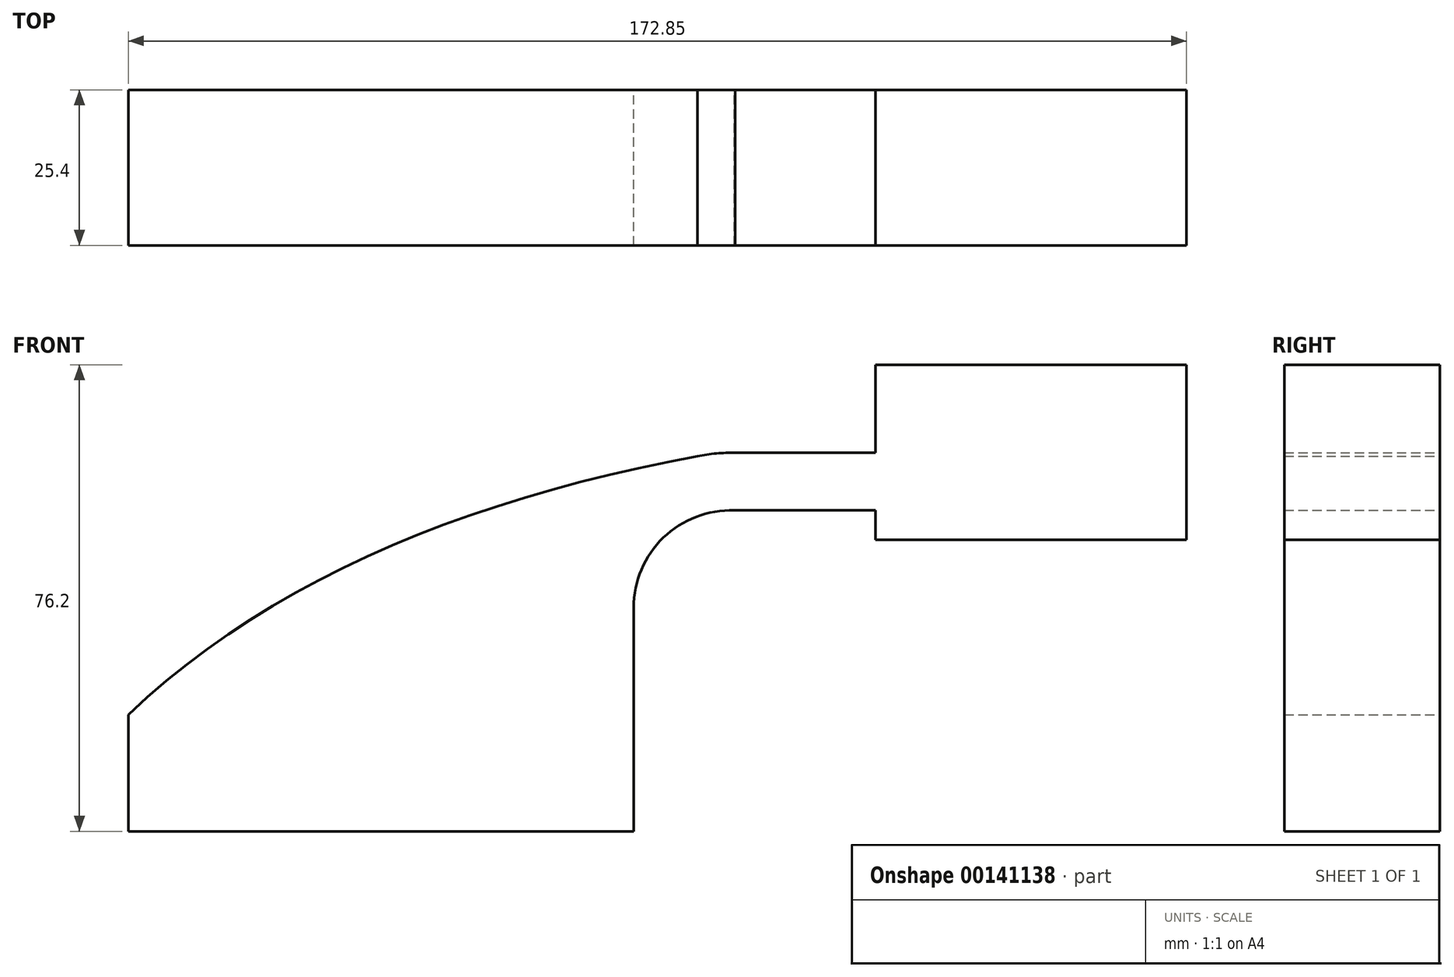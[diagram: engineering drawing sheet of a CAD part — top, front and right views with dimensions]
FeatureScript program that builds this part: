
annotation { "Feature Type Name" : "Feature", "Feature Type Description" : "" }
export const myFeature = defineFeature(function(context is Context, id is Id, definition is map)
    precondition{}
    {
        {
            var Q0;
            Q0=qCreatedBy(makeId("Front.planeOp"),FACE);
            var sketch = newSketch(context, id + "F0", { "sketchPlane" : qUnion([Q0])});
            skLineSegment(sketch, "E0.bottom", {"start": v(0, 0) * mm, "end": v(-82.55, 0) * mm});
            skLineSegment(sketch, "E0.top", {"start": v(0, 19.05) * mm, "end": v(-82.55, 19.05) * mm});
            skLineSegment(sketch, "E0.left", {"start": v(0, 0) * mm, "end": v(0, 19.05) * mm});
            skLineSegment(sketch, "E0.right", {"start": v(-82.55, 0) * mm, "end": v(-82.55, 19.05) * mm});
            skLineSegment(sketch, "E1.bottom", {"start": v(39.5, 47.63) * mm, "end": v(90.3, 47.63) * mm});
            skLineSegment(sketch, "E1.top", {"start": v(39.5, 76.2) * mm, "end": v(90.3, 76.2) * mm});
            skLineSegment(sketch, "E1.left", {"start": v(39.5, 47.63) * mm, "end": v(39.5, 76.2) * mm});
            skLineSegment(sketch, "E1.right", {"start": v(90.3, 47.63) * mm, "end": v(90.3, 76.2) * mm});
            skLineSegment(sketch, "E2", {"start": v(0, 19.05) * mm, "end": v(0, 36.54) * mm});
            skArc(sketch, "E3", {"start": v(0, 36.54) * mm, "mid": v(4.85, 47.96) * mm, "end": v(16.44, 52.4) * mm});
            skLineSegment(sketch, "E4", {"start": v(16.44, 52.4) * mm, "end": v(53.14, 52.4) * mm});
            skLineSegment(sketch, "E5.0", {"start": v(16.6, 61.81) * mm, "end": v(53.14, 61.81) * mm});
            skArc(sketch, "E5.1", {"start": v(-9.41, 36.54) * mm, "mid": v(-1.75, 54.67) * mm, "end": v(16.6, 61.81) * mm});
            skLineSegment(sketch, "E5.2", {"start": v(-9.41, 19.05) * mm, "end": v(-9.41, 36.54) * mm});
            skFitSpline(sketch, "E6", {"points": [v(-82.55, 19.05) * mm, v(12.33, 61.57) * mm], "startDerivative": vector(70.49, 67.1) * mm, "endDerivative": vector(115.35, 20.45) * mm});
            skSolve(sketch);
        }
        {
            var Q0;
            Q0 = qSketchRegion(id + "F0", true);
            extrude(context, id + "F1", {"entities" : qUnion([Q0]), "depth" : 25.4 * mm});
        }
    });
